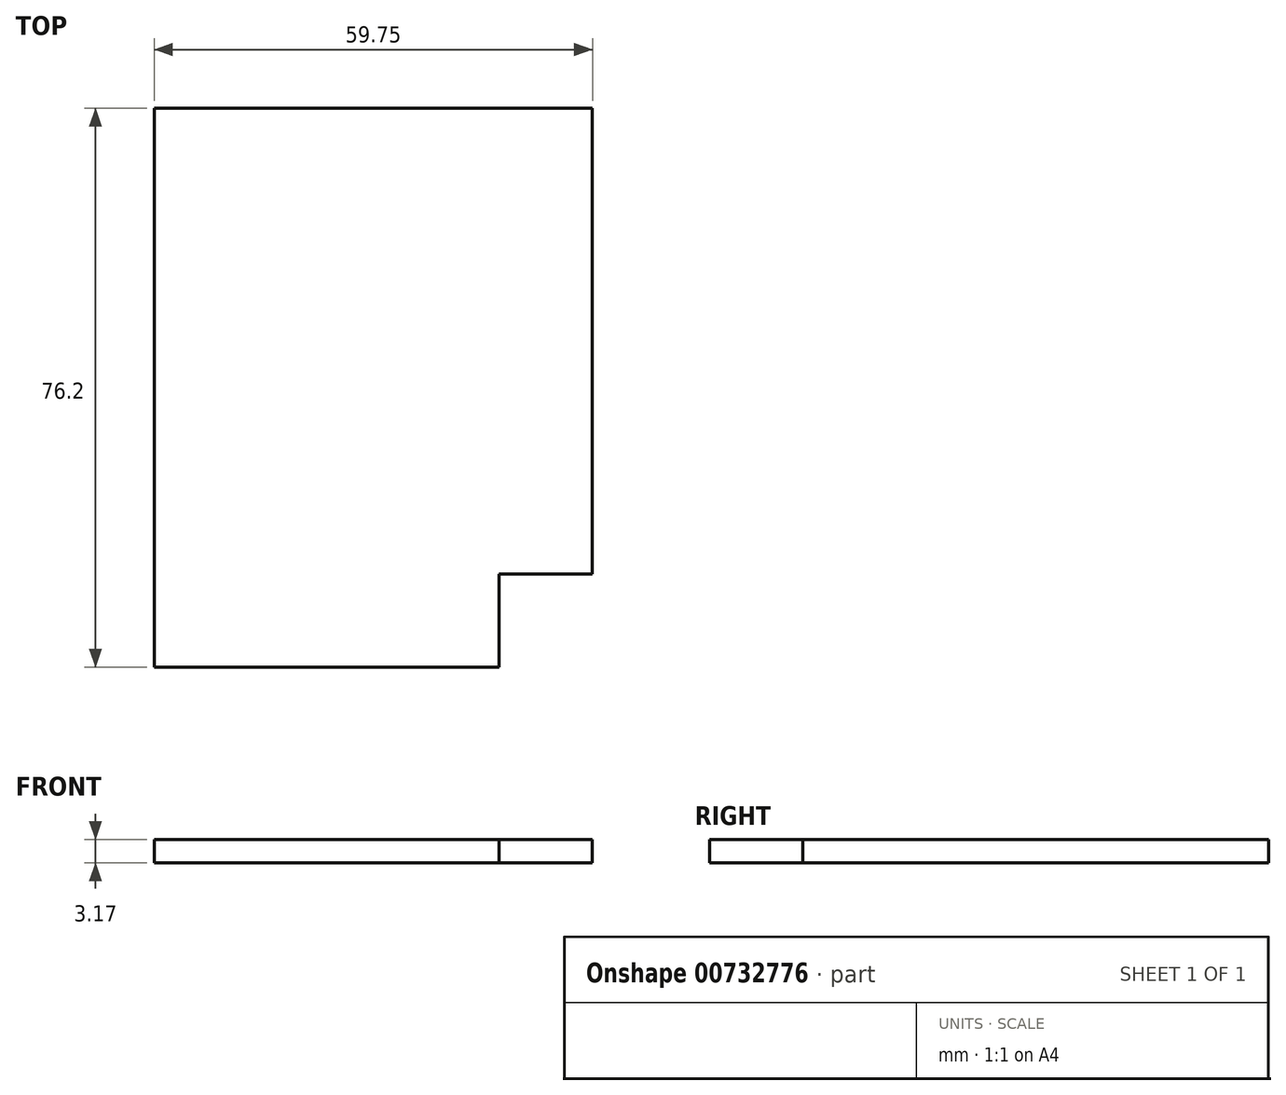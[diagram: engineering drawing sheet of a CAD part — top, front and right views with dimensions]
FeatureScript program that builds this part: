
annotation { "Feature Type Name" : "Feature", "Feature Type Description" : "" }
export const myFeature = defineFeature(function(context is Context, id is Id, definition is map)
    precondition{}
    {
        {
            var Q0;
            Q0=qCreatedBy(makeId("Top.planeOp"),FACE);
            var sketch = newSketch(context, id + "F0", { "sketchPlane" : qUnion([Q0])});
            skLineSegment(sketch, "E0", {"start": v(-36.3, -40.4) * mm, "end": v(-36.3, 35.8) * mm});
            skLineSegment(sketch, "E1.MirrorCS", {"start": v(23.46, -40.4) * mm, "end": v(23.46, 35.8) * mm});
            skLineSegment(sketch, "E2", {"start": v(-36.3, 35.8) * mm, "end": v(23.46, 35.8) * mm});
            skLineSegment(sketch, "E3", {"start": v(23.46, -40.4) * mm, "end": v(-36.3, -40.4) * mm});
            skLineSegment(sketch, "E4", {"start": v(23.46, -40.4) * mm, "end": v(23.46, -27.7) * mm});
            skLineSegment(sketch, "E5", {"start": v(23.46, -27.7) * mm, "end": v(10.76, -27.7) * mm});
            skLineSegment(sketch, "E6", {"start": v(10.76, -27.7) * mm, "end": v(10.76, -40.4) * mm});
            skLineSegment(sketch, "E7.MirrorCS", {"start": v(23.46, 23.1) * mm, "end": v(10.76, 23.1) * mm});
            skLineSegment(sketch, "E8.MirrorCS", {"start": v(10.76, 23.1) * mm, "end": v(10.76, 35.8) * mm});
            skLineSegment(sketch, "E9.MirrorCS", {"start": v(-36.3, 23.1) * mm, "end": v(-23.6, 23.1) * mm});
            skLineSegment(sketch, "E10.MirrorCS", {"start": v(-23.6, 23.1) * mm, "end": v(-23.6, 35.8) * mm});
            skSolve(sketch);
        }
        {
            var Q0;
            {var subQ4=sQuery(id+"F0.wireOp",EDGE,"E5");Q0=makeQuery(id+"F0.imprint","IMPRINT",FACE,{"disambiguationData":[TD([[makeQuery(id+"F0.imprint","IMPRINT",EDGE,{"derivedFrom":subQ4}),-1.0]])]});}
            var Q1;
            {var subQ3=sQuery(id+"F0.wireOp",EDGE,"E9.MirrorCS");Q1=makeQuery(id+"F0.imprint","IMPRINT",FACE,{"disambiguationData":[TD([[makeQuery(id+"F0.imprint","IMPRINT",EDGE,{"derivedFrom":subQ3}),1.0]])]});}
            var Q2;
            {var subQ3=sQuery(id+"F0.wireOp",EDGE,"E7.MirrorCS");Q2=makeQuery(id+"F0.imprint","IMPRINT",FACE,{"disambiguationData":[TD([[makeQuery(id+"F0.imprint","IMPRINT",EDGE,{"derivedFrom":subQ3}),-1.0]])]});}
            var Q3;
            {var subQ0=sQuery(id+"F0.wireOp",EDGE,"E4");Q3=makeQuery(id+"F0.imprint","IMPRINT",FACE,{"disambiguationData":[TD([[makeQuery(id+"F0.imprint","IMPRINT",EDGE,{"derivedFrom":subQ0}),1.0]])]});}
            extrude(context, id + "F1", {"entities" : qUnion([Q0, Q1, Q2, Q3]), "depth" : 3.17 * mm, "offsetDistance" : 25.4 * mm});
        }
    });
